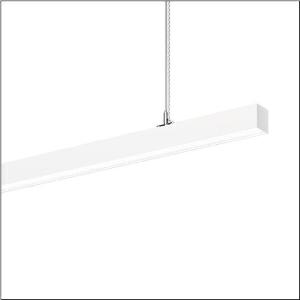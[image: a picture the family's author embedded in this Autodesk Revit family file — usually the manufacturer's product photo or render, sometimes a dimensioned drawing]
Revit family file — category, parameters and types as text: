
# Revit family: silica_r__21_51mx30da44wb_0345
name_source: partatom
category: Lighting Fixtures
units: mm (PartAtom-declared; Revit-internal decimal feet)

## family parameters
Cut with Voids When Loaded = No
Host = Face
Light Source = No
Part Type = Normal
Room Calculation Point = No
Round Connector Dimension = Use Diameter
Shared = No

## types (1)
- --- (1 x LED, 4210 lm, 26 W, 4000K)
    Apparent Load = 26 VA
    CIE Flux Codes = 47 79 96 57 100
    Color Rendering = 80
    Color Temperature = 4000K
    Default Elevation = 1800 mm
    Description = Silica® 21, office luminaire, primary optical cover: cover, of PMMA, opal, light emission: direct/indirect distribution, primary light characteristic: symmetric, installation type: suspended mounting, LED, rated luminous flux: 4.210lm, luminous efficacy: 162lm/W, light colour: 840, colour temperature: 4000K, with terminal, 3+2-pole, max. 2.5mm², mains connection: 220..240V, AC, 50/60Hz, rated input power: 26W, luminaire housing, of aluminium, traffic white (RAL 9016), length: 1.204mm, width: 53mm, height: 53mm, protection rating (complete): IP20, insulation class (complete): insulation class I (protective earthing), certification: CE, permissible operating ambient temperature: 0..+35°C, standard: EN 50419, packaging unit: 1 piece
    Height = 53 mm
    Lamp = 1 x LED
    Lamp Light Flux = 4210 lm
    Lamp Power = 26 W
    Lamp count = 1
    Length = 1204 mm
    Luminous efficacy = 162 lm/W
    Manufacturer = Siteco
    ModVariant = No
    Model = 51MX30DA44WB
    Mounting Place = Ceiling
    Mounting Type = Pendant
    Number of Poles = 1
    OnlyDefault = Yes
    Power Factor = 1
    Product Name = Silica® 21
    Product group = office luminaire | ceiling pendant
    ProductGroupID = 902
    Protection Class = Protection class I
    Protection Degree = IP 20
    RLX_Detail_Level = 1
    RLX_Emergency_Light_Flux = 0 lm
    RLX_Emergency_Type = 0
    RLX_Emergency_Type_DB = No
    RlxData = <blob elided: 21193 chars, md5=1f29cb2a>
    Socket = socket
    Standby Power = 0 W
    System Light Flux = 4210 lm
    System Power = 26 W
    Type Comments = factory setting: luminous flux: 100 % | dim-lin: 254 | 218 mA
    Type Image = l_1335916.jpg
    URL = http://relux.com
    VarID = @adj_086361
    Voltage = 0 V
    Weight = 0.00 kg
    Width = 53 mm

## geometry (parser evidence)
native form markers: Blend x4, Sweep x13
no freeform markers — native parametric forms only
